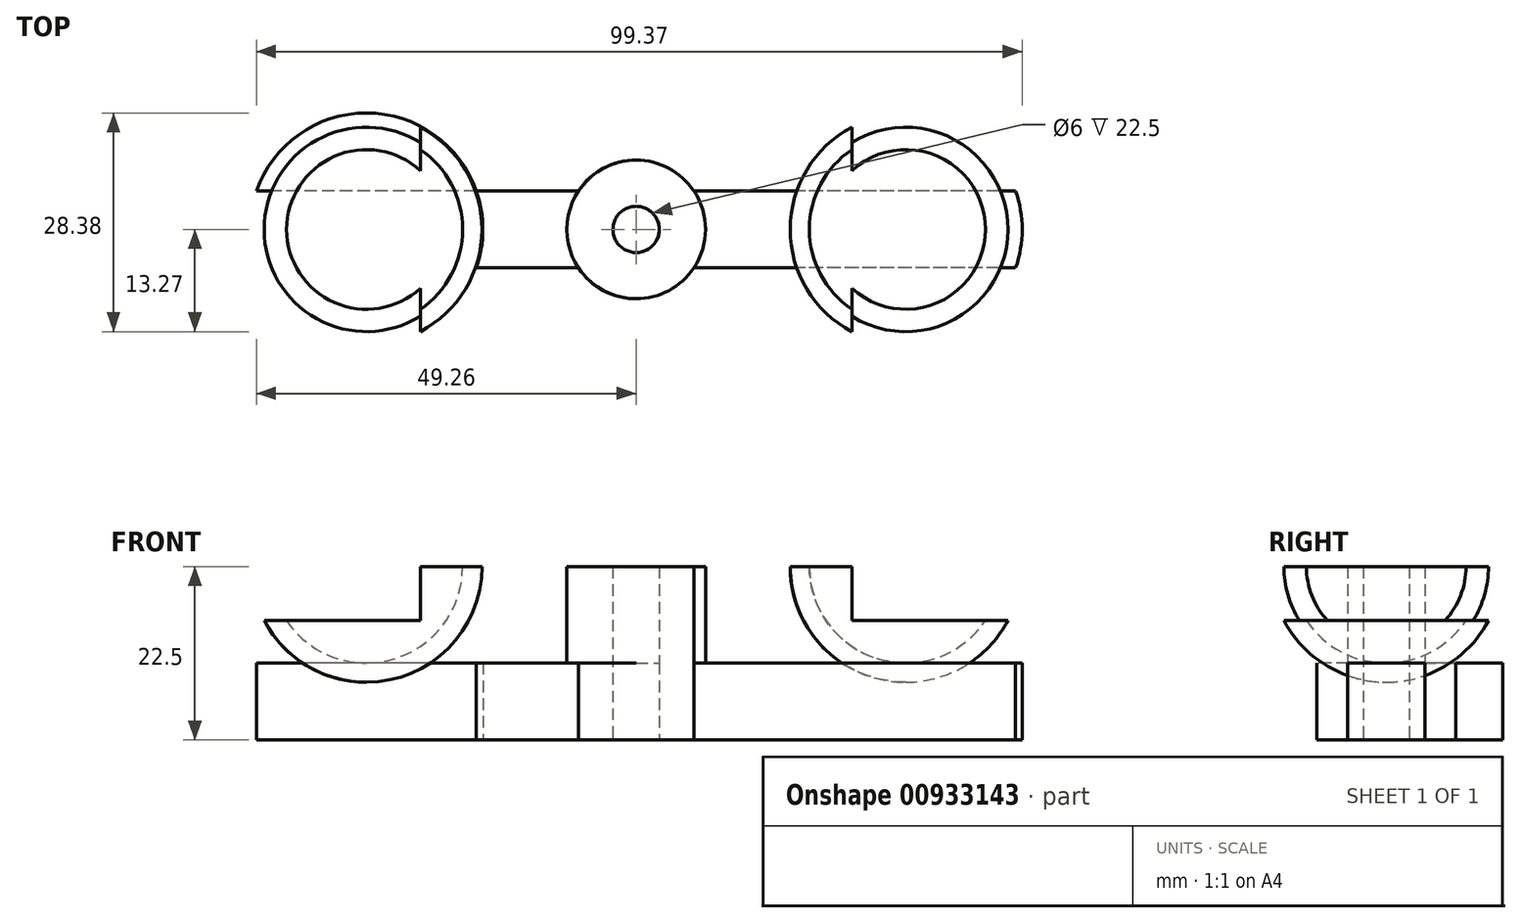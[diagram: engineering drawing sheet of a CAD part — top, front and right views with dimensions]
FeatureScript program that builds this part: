
annotation { "Feature Type Name" : "Feature", "Feature Type Description" : "" }
export const myFeature = defineFeature(function(context is Context, id is Id, definition is map)
    precondition{}
    {
        {
            var Q0;
            Q0=qCreatedBy(makeId("Front.planeOp"),FACE);
            var sketch = newSketch(context, id + "F0", { "sketchPlane" : qUnion([Q0])});
            skLineSegment(sketch, "E0", {"start": v(-35, 0) * mm, "end": v(-35, 31.07) * mm, "construction": true});
            skLineSegment(sketch, "E1", {"start": v(35, 0) * mm, "end": v(35, 31.07) * mm, "construction": true});
            skSolve(sketch);
        }
        {
            var Q0;
            Q0=qCreatedBy(makeId("Top.planeOp"),FACE);
            var sketch = newSketch(context, id + "F1", { "sketchPlane" : qUnion([Q0])});
            skCircle(sketch, "E2", {"center": v(35, 0) * mm, "radius": 12.5 * mm});
            skCircle(sketch, "E3", {"center": v(-35, 0) * mm, "radius": 12.5 * mm});
            skCircle(sketch, "E4", {"center": v(0, 0) * mm, "radius": 3 * mm});
            skCircle(sketch, "E5", {"center": v(0, 0) * mm, "radius": 9 * mm});
            skLineSegment(sketch, "E6", {"start": v(68.91, 0) * mm, "end": v(-65.67, 0) * mm, "construction": true});
            skLineSegment(sketch, "E7", {"start": v(0, 22.53) * mm, "end": v(0, -24.63) * mm, "construction": true});
            skCircle(sketch, "E8", {"center": v(35, 0) * mm, "radius": 15.11 * mm});
            skCircle(sketch, "E9", {"center": v(-35, 0) * mm, "radius": 15.11 * mm});
            skLineSegment(sketch, "E10", {"start": v(49.26, -5) * mm, "end": v(-49.26, -5) * mm});
            skLineSegment(sketch, "E11", {"start": v(49.26, 5) * mm, "end": v(-49.26, 5) * mm});
            skSolve(sketch);
        }
        {
            var Q0;
            {var subQ0=sQuery(id+"F1.wireOp",EDGE,"E11");var subQ1=sQuery(id+"F1.wireOp",EDGE,"E2");var subQ2=makeQuery(id+"F1.imprint","INTERSECT",VERTEX,{"disambiguationData":[OD(1.0)],"derivedFrom":[subQ1,subQ0]});Q0=makeQuery(id+"F1.imprint","IMPRINT",FACE,{"disambiguationData":[TD([[makeQuery(id+"F1.imprint","IMPRINT",EDGE,{"disambiguationData":[TD([[subQ2,1.0]])],"derivedFrom":subQ1}),-1.0]])]});}
            var Q1;
            {var subQ0=sQuery(id+"F1.wireOp",EDGE,"E11");var subQ1=sQuery(id+"F1.wireOp",EDGE,"E3");var subQ2=makeQuery(id+"F1.imprint","INTERSECT",VERTEX,{"disambiguationData":[OD(0.0)],"derivedFrom":[subQ1,subQ0]});Q1=makeQuery(id+"F1.imprint","IMPRINT",FACE,{"disambiguationData":[TD([[makeQuery(id+"F1.imprint","IMPRINT",EDGE,{"disambiguationData":[TD([[subQ2,-1.0]])],"derivedFrom":subQ1}),-1.0]])]});}
            var Q2;
            {var subQ0=sQuery(id+"F1.wireOp",EDGE,"E11");var subQ1=sQuery(id+"F1.wireOp",EDGE,"E3");var subQ2=makeQuery(id+"F1.imprint","INTERSECT",VERTEX,{"disambiguationData":[OD(0.0)],"derivedFrom":[subQ1,subQ0]});Q2=makeQuery(id+"F1.imprint","IMPRINT",FACE,{"disambiguationData":[TD([[makeQuery(id+"F1.imprint","IMPRINT",EDGE,{"disambiguationData":[TD([[subQ2,-1.0]])],"derivedFrom":subQ1}),1.0]])]});}
            var Q3;
            {var subQ0=sQuery(id+"F1.wireOp",EDGE,"E11");var subQ1=sQuery(id+"F1.wireOp",EDGE,"E3");var subQ2=makeQuery(id+"F1.imprint","INTERSECT",VERTEX,{"disambiguationData":[OD(1.0)],"derivedFrom":[subQ1,subQ0]});Q3=makeQuery(id+"F1.imprint","IMPRINT",FACE,{"disambiguationData":[TD([[makeQuery(id+"F1.imprint","IMPRINT",EDGE,{"disambiguationData":[TD([[subQ2,1.0]])],"derivedFrom":subQ1}),-1.0]])]});}
            var Q4;
            {var subQ0=sQuery(id+"F1.wireOp",EDGE,"E11");var subQ1=sQuery(id+"F1.wireOp",EDGE,"E5");var subQ2=makeQuery(id+"F1.imprint","INTERSECT",VERTEX,{"disambiguationData":[OD(0.0)],"derivedFrom":[subQ1,subQ0]});Q4=makeQuery(id+"F1.imprint","IMPRINT",FACE,{"disambiguationData":[TD([[makeQuery(id+"F1.imprint","IMPRINT",EDGE,{"disambiguationData":[TD([[subQ2,-1.0]])],"derivedFrom":subQ1}),-1.0]])]});}
            var Q5;
            Q5=makeQuery(id+"F1.imprint","IMPRINT",FACE,{"disambiguationData":[TD([[makeQuery(id+"F1.imprint","IMPRINT",EDGE,{"derivedFrom":sQuery(id+"F1.wireOp",EDGE,"E4")}),-1.0]])]});
            var Q6;
            {var subQ0=sQuery(id+"F1.wireOp",EDGE,"E11");var subQ1=sQuery(id+"F1.wireOp",EDGE,"E5");var subQ2=makeQuery(id+"F1.imprint","INTERSECT",VERTEX,{"disambiguationData":[OD(1.0)],"derivedFrom":[subQ1,subQ0]});Q6=makeQuery(id+"F1.imprint","IMPRINT",FACE,{"disambiguationData":[TD([[makeQuery(id+"F1.imprint","IMPRINT",EDGE,{"disambiguationData":[TD([[subQ2,1.0]])],"derivedFrom":subQ1}),-1.0]])]});}
            var Q7;
            {var subQ0=sQuery(id+"F1.wireOp",EDGE,"E11");var subQ1=sQuery(id+"F1.wireOp",EDGE,"E2");var subQ2=makeQuery(id+"F1.imprint","INTERSECT",VERTEX,{"disambiguationData":[OD(0.0)],"derivedFrom":[subQ1,subQ0]});Q7=makeQuery(id+"F1.imprint","IMPRINT",FACE,{"disambiguationData":[TD([[makeQuery(id+"F1.imprint","IMPRINT",EDGE,{"disambiguationData":[TD([[subQ2,-1.0]])],"derivedFrom":subQ1}),-1.0]])]});}
            var Q8;
            {var subQ0=sQuery(id+"F1.wireOp",EDGE,"E11");var subQ1=sQuery(id+"F1.wireOp",EDGE,"E2");var subQ2=makeQuery(id+"F1.imprint","INTERSECT",VERTEX,{"disambiguationData":[OD(0.0)],"derivedFrom":[subQ1,subQ0]});Q8=makeQuery(id+"F1.imprint","IMPRINT",FACE,{"disambiguationData":[TD([[makeQuery(id+"F1.imprint","IMPRINT",EDGE,{"disambiguationData":[TD([[subQ2,-1.0]])],"derivedFrom":subQ1}),1.0]])]});}
            var Q9;
            {var subQ0=sQuery(id+"F1.wireOp",EDGE,"E11");var subQ1=sQuery(id+"F1.wireOp",EDGE,"E5");var subQ2=makeQuery(id+"F1.imprint","INTERSECT",VERTEX,{"disambiguationData":[OD(0.0)],"derivedFrom":[subQ1,subQ0]});Q9=makeQuery(id+"F1.imprint","IMPRINT",FACE,{"disambiguationData":[TD([[makeQuery(id+"F1.imprint","IMPRINT",EDGE,{"disambiguationData":[TD([[subQ2,1.0]])],"derivedFrom":subQ1}),1.0]])]});}
            var Q10;
            {var subQ0=sQuery(id+"F1.wireOp",EDGE,"E10");var subQ1=sQuery(id+"F1.wireOp",EDGE,"E5");var subQ2=makeQuery(id+"F1.imprint","INTERSECT",VERTEX,{"disambiguationData":[OD(0.0)],"derivedFrom":[subQ1,subQ0]});Q10=makeQuery(id+"F1.imprint","IMPRINT",FACE,{"disambiguationData":[TD([[makeQuery(id+"F1.imprint","IMPRINT",EDGE,{"disambiguationData":[TD([[subQ2,-1.0]])],"derivedFrom":subQ1}),1.0]])]});}
            extrude(context, id + "F2", {"entities" : qUnion([Q0, Q1, Q2, Q3, Q4, Q5, Q6, Q7, Q8, Q9, Q10]), "depth" : 10 * mm, "offsetDistance" : 25 * mm});
        }
        {
            var Q0;
            Q0=qCreatedBy(makeId("Front.planeOp"),FACE);
            var sketch = newSketch(context, id + "F3", { "sketchPlane" : qUnion([Q0])});
            skArc(sketch, "E12", {"start": v(20, 22.5) * mm, "mid": v(24.4, 11.9) * mm, "end": v(35, 7.5) * mm});
            skArc(sketch, "E13", {"start": v(-50, 22.5) * mm, "mid": v(-45.6, 11.9) * mm, "end": v(-35, 7.5) * mm});
            skArc(sketch, "E14", {"start": v(22.5, 22.5) * mm, "mid": v(26.16, 13.66) * mm, "end": v(35, 10) * mm});
            skArc(sketch, "E15", {"start": v(-47.5, 22.5) * mm, "mid": v(-43.84, 13.66) * mm, "end": v(-35, 10) * mm});
            skLineSegment(sketch, "E16.trimOffspring", {"start": v(-47.5, 22.5) * mm, "end": v(-50, 22.5) * mm});
            skLineSegment(sketch, "E17.trimOffspring", {"start": v(22.5, 22.5) * mm, "end": v(20, 22.5) * mm});
            skLineSegment(sketch, "E18", {"start": v(-35, 10) * mm, "end": v(-35, 7.5) * mm});
            skLineSegment(sketch, "E19", {"start": v(35, 10) * mm, "end": v(35, 7.5) * mm});
            skPoint(sketch, "E20.start.orphan", {"position": v(50, 22.5) * mm});
            skLineSegment(sketch, "E21", {"start": v(35, 22.5) * mm, "end": v(35, 0) * mm, "construction": true});
            skSolve(sketch);
        }
        {
            var Q0;
            Q0=makeQuery(id+"F3.imprint","IMPRINT",FACE,{"disambiguationData":[TD([[makeQuery(id+"F3.imprint","IMPRINT",EDGE,{"derivedFrom":sQuery(id+"F3.wireOp",EDGE,"E13")}),1.0]])]});
            var Q1;
            Q1=sQuery(id+"F0.wireOp",EDGE,"E0");
            revolve(context, id + "F4", {"surfaceOperationType" : NewSurfaceOperationType.NEW, "entities" : qUnion([Q0]), "axis" : qUnion([Q1]), "revolveType" : RevolveType.FULL});
        }
        {
            var Q0;
            Q0=makeQuery(id+"F3.imprint","IMPRINT",FACE,{"disambiguationData":[TD([[makeQuery(id+"F3.imprint","IMPRINT",EDGE,{"derivedFrom":sQuery(id+"F3.wireOp",EDGE,"E12")}),1.0]])]});
            var Q1;
            Q1=sQuery(id+"F3.wireOp",EDGE,"E21");
            revolve(context, id + "F5", {"surfaceOperationType" : NewSurfaceOperationType.NEW, "entities" : qUnion([Q0]), "axis" : qUnion([Q1]), "revolveType" : RevolveType.FULL});
        }
        {
            var Q0;
            Q0=makeQuery(id+"F5.opRevolve","SWEPT_FACE",FACE,{"disambiguationData":[OSD([sQuery(id+"F3.wireOp",EDGE,"E17.trimOffspring")])]});
            var sketch = newSketch(context, id + "F6", { "sketchPlane" : qUnion([Q0])});
            skLineSegment(sketch, "E22", {"start": v(28, 0) * mm, "end": v(28, 25.67) * mm});
            skLineSegment(sketch, "E23", {"start": v(28, 25.67) * mm, "end": v(60.4, 25.67) * mm});
            skLineSegment(sketch, "E24", {"start": v(60.4, 25.67) * mm, "end": v(60.4, -23.48) * mm});
            skLineSegment(sketch, "E25", {"start": v(60.4, -23.48) * mm, "end": v(28, -23.48) * mm});
            skLineSegment(sketch, "E26", {"start": v(28, -23.48) * mm, "end": v(28, 0) * mm});
            skPoint(sketch, "E27.start.orphan", {"position": v(35, 0) * mm});
            skLineSegment(sketch, "E28", {"start": v(-28, 25.67) * mm, "end": v(-28, -23.48) * mm});
            skLineSegment(sketch, "E29", {"start": v(-28, -23.48) * mm, "end": v(-62.5, -23.48) * mm});
            skLineSegment(sketch, "E30", {"start": v(-62.5, -23.48) * mm, "end": v(-62.5, 25.67) * mm});
            skLineSegment(sketch, "E31", {"start": v(-62.5, 25.67) * mm, "end": v(-28, 25.67) * mm});
            skSolve(sketch);
        }
        {
            var Q0;
            {var subQ1=sQuery(id+"F6.wireOp",EDGE,"E23");Q0=makeQuery(id+"F6.imprint","IMPRINT",FACE,{"disambiguationData":[TD([[makeQuery(id+"F6.imprint","IMPRINT",EDGE,{"derivedFrom":subQ1}),-1.0]])]});}
            var Q1;
            Q1=makeQuery(id+"F6.imprint","IMPRINT",FACE,{"disambiguationData":[TD([[makeQuery(id+"F6.imprint","IMPRINT",EDGE,{"derivedFrom":sQuery(id+"F6.wireOp",EDGE,"E28")}),-1.0]])]});
            var Q2;
            {var subQ0=sQuery(id+"F6.wireOp",EDGE,"E26");var subQ1=sQuery(id+"F6.wireOp",EDGE,"E22");var subQ2=makeQuery(id+"F6.imprint","INTERSECT",VERTEX,{"derivedFrom":[subQ1,subQ0]});Q2=makeQuery(id+"F6.imprint","IMPRINT",FACE,{"disambiguationData":[TD([[makeQuery(id+"F6.imprint","IMPRINT",EDGE,{"disambiguationData":[TD([[subQ2,-1.0]])],"derivedFrom":subQ1}),-1.0]])]});}
            var Q3;
            {var subQ0=sQuery(id+"F6.wireOp",EDGE,"E22");var subQ1=sQuery(id+"F3.wireOp",EDGE,"E17.trimOffspring");var subQ2=makeQuery(id+"F5.opRevolve","SWEPT_EDGE",EDGE,{"disambiguationData":[OSD([sQuery(id+"F3.wireOp",EDGE,"E12"),subQ1])]});var subQ3=makeQuery(id+"F6.imprint","INTERSECT",VERTEX,{"derivedFrom":[subQ2,subQ0]});Q3=makeQuery(id+"F6.imprint","IMPRINT",FACE,{"disambiguationData":[TD([[makeQuery(id+"F6.imprint","IMPRINT",EDGE,{"disambiguationData":[TD([[subQ3,1.0]])],"derivedFrom":subQ0}),-1.0]])]});}
            extrude(context, id + "F7", {"entities" : qUnion([Q0, Q1, Q2, Q3]), "operationType" : NewBodyOperationType.REMOVE, "oppositeDirection" : true, "depth" : 7 * mm, "offsetDistance" : 25 * mm});
        }
        {
            var Q0;
            {var subQ0=sQuery(id+"F1.wireOp",EDGE,"E10");var subQ1=sQuery(id+"F1.wireOp",EDGE,"E5");var subQ3=sQuery(id+"F1.wireOp",EDGE,"E8");var subQ11=sQuery(id+"F1.wireOp",EDGE,"E11");var subQ15=sQuery(id+"F1.wireOp",EDGE,"E4");var subQ16=makeQuery(id+"F2.opExtrude","SWEPT_FACE",FACE,{"disambiguationData":[OSD([subQ15])]});var subQ17=sQuery(id+"F1.wireOp",EDGE,"E9");Q0=makeQuery(id+"F5.boolean.opBoolean","SPLIT",FACE,{"disambiguationData":[TD([subQ16])],"derivedFrom":makeQuery(id+"F4.boolean.opBoolean","SPLIT",FACE,{"disambiguationData":[TD([subQ16])],"derivedFrom":makeQuery(id+"F2.opExtrude","CAP_FACE",FACE,{"disambiguationData":[OSD([subQ15,subQ1,subQ3,subQ17,subQ0,subQ11])],"isStart":false})})});}
            var sketch = newSketch(context, id + "F8", { "sketchPlane" : qUnion([Q0])});
            skCircle(sketch, "E32", {"center": v(35.03, 0) * mm, "radius": 12.5 * mm});
            skCircle(sketch, "E33", {"center": v(-37.9, 0) * mm, "radius": 12.5 * mm});
            skCircle(sketch, "E34", {"center": v(0.03, 0) * mm, "radius": 3 * mm});
            skCircle(sketch, "E35", {"center": v(0.03, 0) * mm, "radius": 9 * mm});
            skLineSegment(sketch, "E36", {"start": v(68.94, 0) * mm, "end": v(-65.64, 0) * mm, "construction": true});
            skLineSegment(sketch, "E37", {"start": v(0.03, 22.53) * mm, "end": v(0.03, -24.63) * mm, "construction": true});
            skCircle(sketch, "E38", {"center": v(35.03, 0) * mm, "radius": 15.11 * mm});
            skCircle(sketch, "E39", {"center": v(-37.9, 0) * mm, "radius": 15.11 * mm});
            skLineSegment(sketch, "E40", {"start": v(46.36, -10) * mm, "end": v(-49.24, -10) * mm});
            skLineSegment(sketch, "E41", {"start": v(46.36, 10) * mm, "end": v(-49.24, 10) * mm});
            skSolve(sketch);
        }
        {
            var Q0;
            {var subQ21=sQuery(id+"F8.wireOp",EDGE,"E34");var subQ22=makeQuery(id+"F2.opExtrude","CAP_EDGE",EDGE,{"disambiguationData":[OSD([sQuery(id+"F1.wireOp",EDGE,"E4")])],"isStart":false});var subQ23=makeQuery(id+"F8.imprint","INTERSECT",VERTEX,{"disambiguationData":[OD(0.0)],"derivedFrom":[subQ22,subQ21]});Q0=makeQuery(id+"F8.imprint","IMPRINT",FACE,{"disambiguationData":[TD([[makeQuery(id+"F8.imprint","IMPRINT",EDGE,{"disambiguationData":[TD([[subQ23,-1.0]])],"derivedFrom":subQ21}),-1.0]])]});}
            extrude(context, id + "F9", {"entities" : qUnion([Q0]), "operationType" : NewBodyOperationType.ADD, "depth" : 12.5 * mm, "offsetDistance" : 25 * mm});
        }
    });
